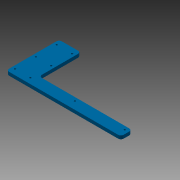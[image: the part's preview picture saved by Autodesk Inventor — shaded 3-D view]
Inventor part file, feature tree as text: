
AUTODESK INVENTOR PART (.ipt)
format: ipt  version: 2013 (Build 170138000, 138)  size: 99,840 bytes
history: native  units: mm
features: extrude x1, sketch x1
ambient origin geometry x8: Origin, YZ Plane, XZ Plane, XY Plane, X Axis, Y Axis, Z Axis, Center Point
bodies: Solid1 (feature_tree)
feature tree (2):
  extrude  "Extrusion1"  [1 undecoded]
  sketch  "Sketch1"  dims[d0=6.0mm d1=0.0mm]
note: 1 required parameter value undecoded (feature->parameter linkage not recoverable at this tier; creation-order binding heuristic only, values carry confidence <= 0.55)
